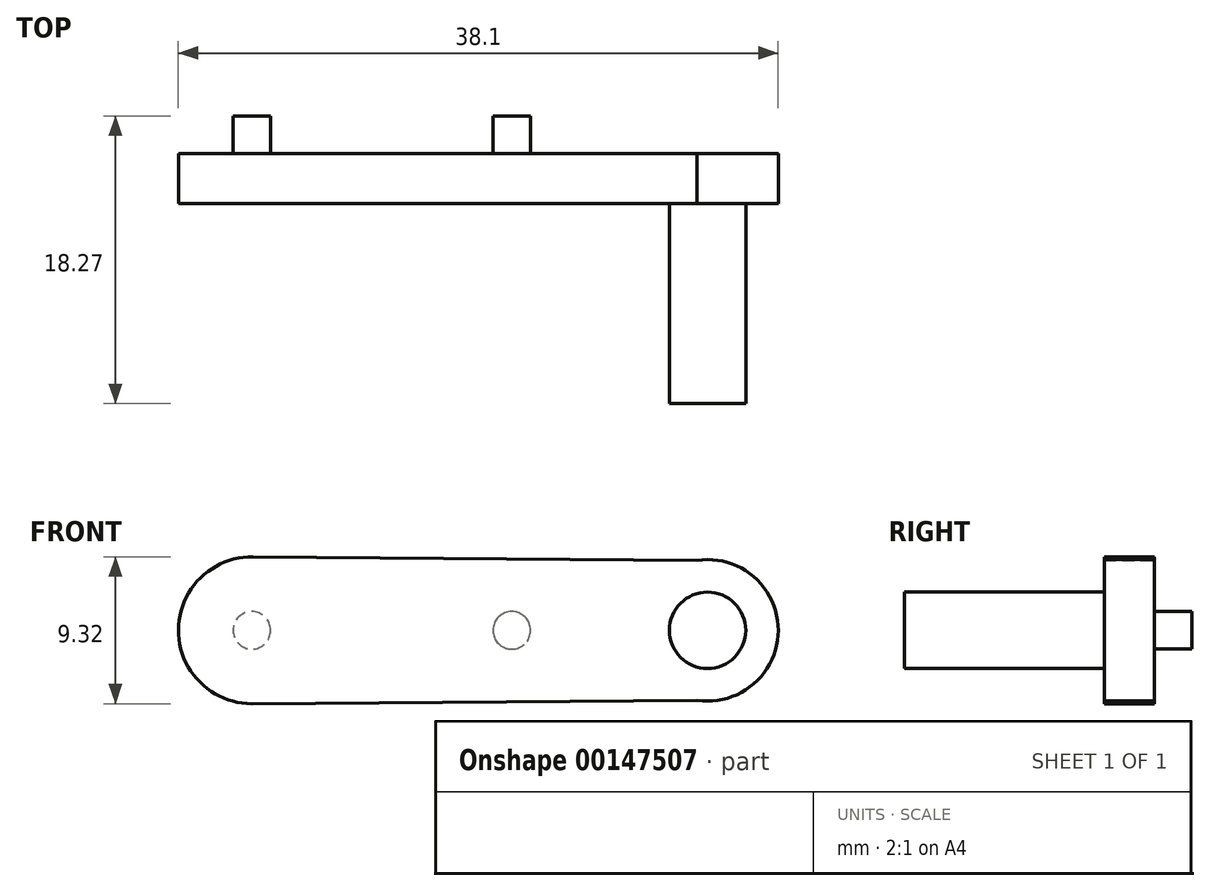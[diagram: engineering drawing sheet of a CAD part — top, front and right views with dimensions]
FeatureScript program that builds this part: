
annotation { "Feature Type Name" : "Feature", "Feature Type Description" : "" }
export const myFeature = defineFeature(function(context is Context, id is Id, definition is map)
    precondition{}
    {
        {
            var Q0;
            Q0=qCreatedBy(makeId("Front.planeOp"),FACE);
            var sketch = newSketch(context, id + "F0", { "sketchPlane" : qUnion([Q0])});
            skArc(sketch, "E0", {"start": v(-28.87, 4.66) * mm, "mid": v(-33.6, 0.04) * mm, "end": v(-28.94, -4.66) * mm});
            skLineSegment(sketch, "E1", {"start": v(-28.94, 4.66) * mm, "end": v(0, 4.44) * mm});
            skLineSegment(sketch, "E2", {"start": v(-28.94, -4.66) * mm, "end": v(0, -4.44) * mm});
            skPoint(sketch, "E3.center.orphan", {"position": v(0, 0) * mm});
            skArc(sketch, "E4", {"start": v(-0.66, -4.45) * mm, "mid": v(4.5, 0) * mm, "end": v(-0.66, 4.45) * mm});
            skSolve(sketch);
        }
        {
            var Q0;
            Q0 = qSketchRegion(id + "F0", true);
            extrude(context, id + "F1", {"entities" : qUnion([Q0]), "depth" : 3.17 * mm});
        }
        {
            var Q0;
            Q0=makeQuery(id+"F1.opExtrude","CAP_FACE",FACE,{"disambiguationData":[OSD([sQuery(id+"F0.wireOp",EDGE,"E0"),sQuery(id+"F0.wireOp",EDGE,"E1"),sQuery(id+"F0.wireOp",EDGE,"E2"),sQuery(id+"F0.wireOp",EDGE,"E4")])],"isStart":false});
            var sketch = newSketch(context, id + "F2", { "sketchPlane" : qUnion([Q0])});
            skCircle(sketch, "E5", {"center": v(0, 0) * mm, "radius": 2.43 * mm});
            skSolve(sketch);
        }
        {
            var Q0;
            Q0 = qSketchRegion(id + "F2", true);
            extrude(context, id + "F3", {"entities" : qUnion([Q0]), "operationType" : NewBodyOperationType.ADD, "depth" : 12.7 * mm});
        }
        {
            var Q0;
            Q0=makeQuery(id+"F1.opExtrude","CAP_FACE",FACE,{"disambiguationData":[OSD([sQuery(id+"F0.wireOp",EDGE,"E0"),sQuery(id+"F0.wireOp",EDGE,"E1"),sQuery(id+"F0.wireOp",EDGE,"E2"),sQuery(id+"F0.wireOp",EDGE,"E4")])],"isStart":true});
            var sketch = newSketch(context, id + "F4", { "sketchPlane" : qUnion([Q0])});
            skCircle(sketch, "E6", {"center": v(28.94, 0) * mm, "radius": 1.2 * mm});
            skCircle(sketch, "E7", {"center": v(12.43, 0) * mm, "radius": 1.2 * mm});
            skSolve(sketch);
        }
        {
            var Q0;
            Q0 = qSketchRegion(id + "F4", true);
            extrude(context, id + "F5", {"entities" : qUnion([Q0]), "operationType" : NewBodyOperationType.ADD, "depth" : 2.4 * mm});
        }
    });
